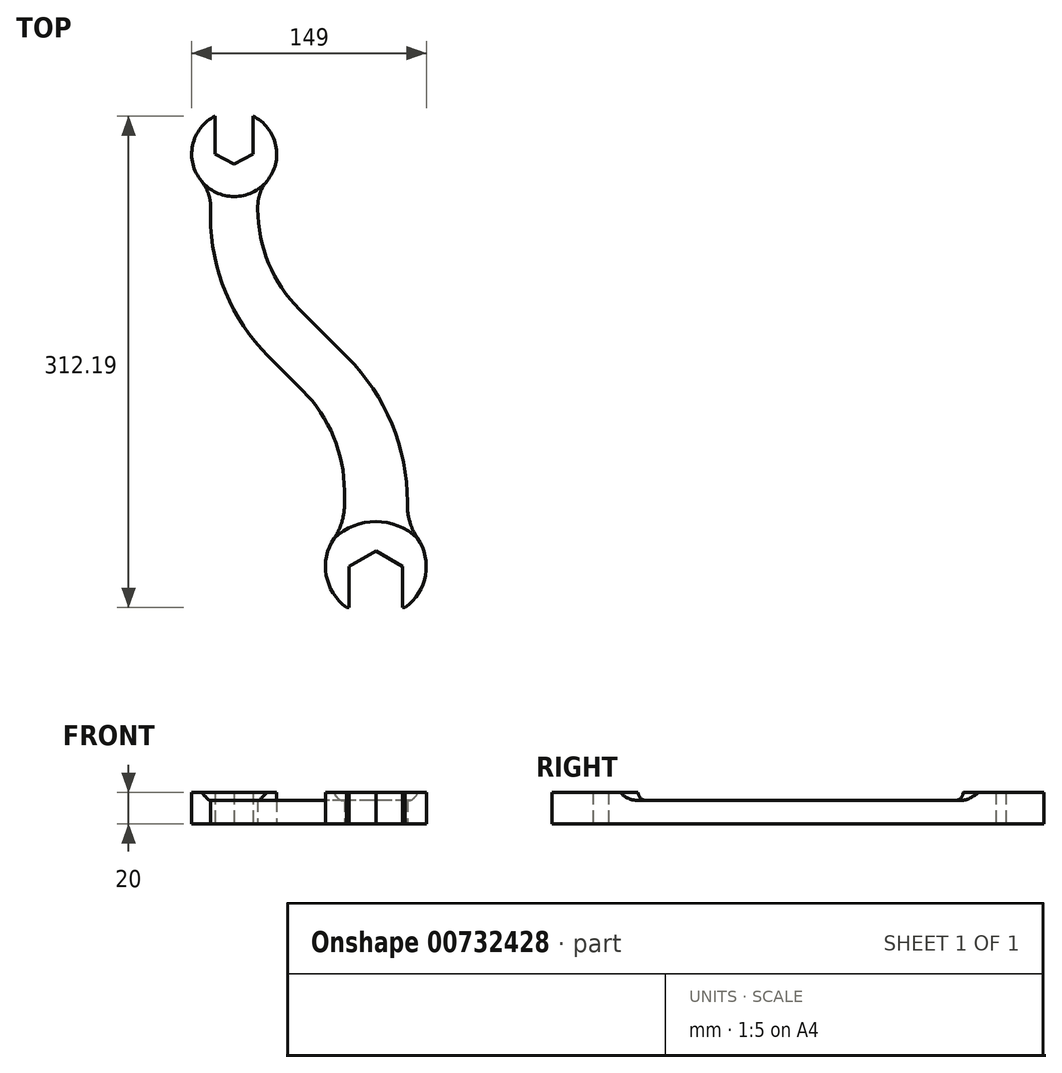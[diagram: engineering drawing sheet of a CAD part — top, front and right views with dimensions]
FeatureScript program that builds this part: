
annotation { "Feature Type Name" : "Feature", "Feature Type Description" : "" }
export const myFeature = defineFeature(function(context is Context, id is Id, definition is map)
    precondition{}
    {
        {
            var Q0;
            Q0=qCreatedBy(makeId("Top.planeOp"),FACE);
            var sketch = newSketch(context, id + "F0", { "sketchPlane" : qUnion([Q0])});
            skArc(sketch, "E0.cCircle", {"start": v(17, 0) * mm, "mid": v(0, 17) * mm, "end": v(-17, 0) * mm, "construction": true});
            skLineSegment(sketch, "E0.0", {"start": v(17, 9.81) * mm, "end": v(17, -16.19) * mm});
            skLineSegment(sketch, "E0.3", {"start": v(-17, -16.19) * mm, "end": v(-17, 9.81) * mm});
            skLineSegment(sketch, "E0.4", {"start": v(-17, 9.81) * mm, "end": v(0, 19.63) * mm});
            skLineSegment(sketch, "E0.5", {"start": v(0, 19.63) * mm, "end": v(17, 9.81) * mm});
            skPoint(sketch, "E0.0.midPoint", {"position": v(17, 0) * mm});
            skArc(sketch, "E1", {"start": v(18.65, -16.19) * mm, "mid": v(31.5, 4.18) * mm, "end": v(26.51, 27.73) * mm});
            skLineSegment(sketch, "E2", {"start": v(-17, 9.81) * mm, "end": v(17, 9.81) * mm, "construction": true});
            skLineSegment(sketch, "E3", {"start": v(-17, -16.19) * mm, "end": v(-18.65, -16.19) * mm});
            skPoint(sketch, "E4.orphan", {"position": v(17, -9.81) * mm});
            skPoint(sketch, "E5.orphan", {"position": v(0, -19.63) * mm});
            skLineSegment(sketch, "E6", {"start": v(17, -16.19) * mm, "end": v(18.65, -16.19) * mm});
            skLineSegment(sketch, "E7", {"start": v(0, 0) * mm, "end": v(0, 138.56) * mm, "construction": true});
            skPoint(sketch, "E7.endSnap0", {"position": v(0, 17) * mm});
            skLineSegment(sketch, "E8", {"start": v(-20, 49) * mm, "end": v(-20, 57.79) * mm});
            skLineSegment(sketch, "E9", {"start": v(20, 49) * mm, "end": v(20, 50.72) * mm});
            skLineSegment(sketch, "E10", {"start": v(-32.38, 49.81) * mm, "end": v(33.68, 49.81) * mm, "construction": true});
            skLineSegment(sketch, "E11", {"start": v(-146.96, 239.81) * mm, "end": v(-33.04, 239.81) * mm, "construction": true});
            skLineSegment(sketch, "E12", {"start": v(-90, 239.81) * mm, "end": v(-90, 281.13) * mm, "construction": true});
            skPoint(sketch, "E13", {"position": v(0, 49.81) * mm});
            skLineSegment(sketch, "E14", {"start": v(0, 49.81) * mm, "end": v(-90, 239.81) * mm, "construction": true});
            skPoint(sketch, "E15", {"position": v(-45, 144.81) * mm});
            skLineSegment(sketch, "E16", {"start": v(-89.72, 100.1) * mm, "end": v(19.7, 209.52) * mm, "construction": true});
            skLineSegment(sketch, "E17", {"start": v(-18.08, 142.64) * mm, "end": v(-48.64, 173.2) * mm});
            skLineSegment(sketch, "E18", {"start": v(-46.36, 121.43) * mm, "end": v(-68.39, 143.45) * mm});
            skLineSegment(sketch, "E19", {"start": v(-105, 238.59) * mm, "end": v(-105, 231.84) * mm});
            skLineSegment(sketch, "E20", {"start": v(-75, 238.59) * mm, "end": v(-75, 236.84) * mm});
            skPoint(sketch, "E21.orphan", {"position": v(-105, 194.11) * mm});
            skPoint(sketch, "E22.orphan", {"position": v(20, 122.51) * mm});
            skPoint(sketch, "E23.orphan", {"position": v(-20, 122.51) * mm});
            skPoint(sketch, "E24.orphan", {"position": v(-75, 194.11) * mm});
            skPoint(sketch, "E25.orphan", {"position": v(-20, 27.9) * mm});
            skPoint(sketch, "E26.orphan", {"position": v(20, 27.9) * mm});
            skLineSegment(sketch, "E27", {"start": v(-146.96, 271.81) * mm, "end": v(-33.04, 271.81) * mm, "construction": true});
            skLineSegment(sketch, "E28", {"start": v(-102, 296) * mm, "end": v(-102, 271.81) * mm});
            skLineSegment(sketch, "E29", {"start": v(-78, 296) * mm, "end": v(-78, 271.81) * mm});
            skPoint(sketch, "E30", {"position": v(-90, 271.81) * mm});
            skArc(sketch, "E31", {"start": v(-102, 296) * mm, "mid": v(-116.42, 277.4) * mm, "end": v(-110.77, 254.56) * mm});
            skLineSegment(sketch, "E32", {"start": v(-78, 271.81) * mm, "end": v(-90, 265.56) * mm});
            skLineSegment(sketch, "E33", {"start": v(-90, 265.56) * mm, "end": v(-102, 271.81) * mm});
            skPoint(sketch, "E34.orphan", {"position": v(-102, 306.21) * mm});
            skPoint(sketch, "E35.orphan", {"position": v(-78, 306.21) * mm});
            skPoint(sketch, "E36.orphan", {"position": v(-105, 260.57) * mm});
            skPoint(sketch, "E37.orphan", {"position": v(-75, 260.57) * mm});
            skArc(sketch, "E38.trimOffspring", {"start": v(-69.23, 254.56) * mm, "mid": v(-63.58, 277.4) * mm, "end": v(-78, 296) * mm});
            skArc(sketch, "E39.trimOffspring", {"start": v(-26.51, 27.73) * mm, "mid": v(-31.5, 4.18) * mm, "end": v(-18.65, -16.19) * mm});
            skPoint(sketch, "E40.visualSharp", {"position": v(-75, 249.37) * mm});
            skArc(sketch, "E40.filletArc", {"start": v(-69.23, 254.56) * mm, "mid": v(-73.51, 247.08) * mm, "end": v(-75, 238.59) * mm});
            skPoint(sketch, "E41.visualSharp", {"position": v(-105, 249.37) * mm});
            skArc(sketch, "E41.filletArc", {"start": v(-105, 238.59) * mm, "mid": v(-106.49, 247.08) * mm, "end": v(-110.77, 254.56) * mm});
            skPoint(sketch, "E42.visualSharp", {"position": v(-20, 34.8) * mm});
            skArc(sketch, "E42.filletArc", {"start": v(-26.51, 27.73) * mm, "mid": v(-21.67, 37.88) * mm, "end": v(-20, 49) * mm});
            skPoint(sketch, "E43.visualSharp", {"position": v(20, 34.8) * mm});
            skArc(sketch, "E43.filletArc", {"start": v(20, 49) * mm, "mid": v(21.67, 37.88) * mm, "end": v(26.51, 27.73) * mm});
            skPoint(sketch, "E44.visualSharp", {"position": v(-20, 95.07) * mm});
            skArc(sketch, "E44.filletArc", {"start": v(-20, 57.79) * mm, "mid": v(-26.85, 92.23) * mm, "end": v(-46.36, 121.43) * mm});
            skPoint(sketch, "E45.visualSharp", {"position": v(20, 104.56) * mm});
            skArc(sketch, "E45.filletArc", {"start": v(20, 50.72) * mm, "mid": v(10.1, 100.46) * mm, "end": v(-18.08, 142.64) * mm});
            skPoint(sketch, "E46.visualSharp", {"position": v(-75, 199.56) * mm});
            skArc(sketch, "E46.filletArc", {"start": v(-75, 236.84) * mm, "mid": v(-68.15, 202.4) * mm, "end": v(-48.64, 173.2) * mm});
            skPoint(sketch, "E47.visualSharp", {"position": v(-105, 180.07) * mm});
            skArc(sketch, "E47.filletArc", {"start": v(-105, 231.84) * mm, "mid": v(-95.48, 184) * mm, "end": v(-68.39, 143.45) * mm});
            skSolve(sketch);
        }
        {
            var Q0;
            Q0 = qSketchRegion(id + "F0", true);
            extrude(context, id + "F1", {"entities" : qUnion([Q0]), "endBound" : BoundingType.SYMMETRIC, "depth" : 20 * mm, "offsetDistance" : 25 * mm});
        }
        {
            var Q0;
            Q0=qCreatedBy(makeId("Top.planeOp"),FACE);
            cPlane(context, id + "F2", {"entities" : qUnion([Q0]), "cplaneType" : CPlaneType.OFFSET, "offset" : 5 * mm, "width" : 150 * mm, "height" : 150 * mm});
        }
        {
            var Q0;
            Q0=qCreatedBy(id+"F2.planeOp",FACE);
            var sketch = newSketch(context, id + "F3", { "sketchPlane" : qUnion([Q0])});
            skArc(sketch, "E48.0", {"start": v(20, 50.72) * mm, "mid": v(10.1, 100.46) * mm, "end": v(-18.08, 142.64) * mm});
            skArc(sketch, "E49.0", {"start": v(-75, 236.84) * mm, "mid": v(-68.15, 202.4) * mm, "end": v(-48.64, 173.2) * mm});
            skLineSegment(sketch, "E50.0", {"start": v(-18.08, 142.64) * mm, "end": v(-48.64, 173.2) * mm});
            skArc(sketch, "E51.0", {"start": v(-20, 57.79) * mm, "mid": v(-26.85, 92.23) * mm, "end": v(-46.36, 121.43) * mm});
            skLineSegment(sketch, "E52.0", {"start": v(-46.36, 121.43) * mm, "end": v(-68.39, 143.45) * mm});
            skArc(sketch, "E53.0", {"start": v(-105, 231.84) * mm, "mid": v(-95.48, 184) * mm, "end": v(-68.39, 143.45) * mm});
            skLineSegment(sketch, "E54.0", {"start": v(-20, 49) * mm, "end": v(-20, 57.79) * mm});
            skArc(sketch, "E55.0", {"start": v(-26.51, 27.73) * mm, "mid": v(-21.67, 37.88) * mm, "end": v(-20, 49) * mm});
            skArc(sketch, "E56.0", {"start": v(20, 49) * mm, "mid": v(21.67, 37.88) * mm, "end": v(26.51, 27.73) * mm});
            skArc(sketch, "E57.0", {"start": v(-69.23, 254.56) * mm, "mid": v(-73.51, 247.08) * mm, "end": v(-75, 238.59) * mm});
            skLineSegment(sketch, "E58.0", {"start": v(-75, 238.59) * mm, "end": v(-75, 236.84) * mm});
            skLineSegment(sketch, "E59.0", {"start": v(-105, 238.59) * mm, "end": v(-105, 231.84) * mm});
            skArc(sketch, "E60.0", {"start": v(-105, 238.59) * mm, "mid": v(-106.49, 247.08) * mm, "end": v(-110.77, 254.56) * mm});
            skArc(sketch, "E61", {"start": v(26.51, 27.73) * mm, "mid": v(0, 38.37) * mm, "end": v(-26.51, 27.73) * mm});
            skLineSegment(sketch, "E62.0", {"start": v(20, 49) * mm, "end": v(20, 50.72) * mm});
            skArc(sketch, "E63.0", {"start": v(-110.77, 254.56) * mm, "mid": v(-90, 244.81) * mm, "end": v(-69.23, 254.56) * mm});
            skPoint(sketch, "E64.orphan", {"position": v(-78, 296) * mm});
            skSolve(sketch);
        }
        {
            var Q0;
            Q0 = qSketchRegion(id + "F3", true);
            extrude(context, id + "F4", {"entities" : qUnion([Q0]), "operationType" : NewBodyOperationType.REMOVE, "depth" : 5 * mm, "offsetDistance" : 25 * mm});
        }
        {
            var Q0;
            Q0=makeQuery(id+"F4.boolean.opBoolean","COPY",EDGE,{"derivedFrom":makeQuery(id+"F4.opExtrude","CAP_EDGE",EDGE,{"disambiguationData":[OSD([sQuery(id+"F3.wireOp",EDGE,"E63.0")])],"isStart":true})});
            var Q1;
            Q1=makeQuery(id+"F8lqRFfdNdjwHrk_1.1.F4.boolean.opBoolean","COPY",EDGE,{"derivedFrom":makeQuery(id+"F8lqRFfdNdjwHrk_1.1.F4.opExtrude","CAP_EDGE",EDGE,{"disambiguationData":[OSD([sQuery(id+"F3.wireOp",EDGE,"E63.0")])],"isStart":true})});
            var Q2;
            Q2=makeQuery(id+"F8lqRFfdNdjwHrk_1.1.F4.boolean.opBoolean","COPY",EDGE,{"derivedFrom":makeQuery(id+"F8lqRFfdNdjwHrk_1.1.F4.opExtrude","CAP_EDGE",EDGE,{"disambiguationData":[OSD([sQuery(id+"F3.wireOp",EDGE,"E61")])],"isStart":true})});
            var Q3;
            Q3=makeQuery(id+"F4.boolean.opBoolean","COPY",EDGE,{"derivedFrom":makeQuery(id+"F4.opExtrude","CAP_EDGE",EDGE,{"disambiguationData":[OSD([sQuery(id+"F3.wireOp",EDGE,"E61")])],"isStart":true})});
            fillet(context, id + "F5", {"entities" : qUnion([Q0, Q1, Q2, Q3]), "radius" : 5 * mm, "tangentPropagation" : true, "allowEdgeOverflow" : false});
        }
    });
